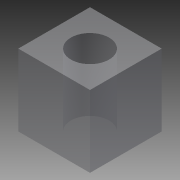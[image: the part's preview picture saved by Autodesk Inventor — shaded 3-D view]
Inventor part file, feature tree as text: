
AUTODESK INVENTOR PART (.ipt)
format: ipt  version: 2013 (Build 170138000, 138)  size: 76,800 bytes
history: native  units: in
note: dims shown in document units (in); Inventor stores cm internally (conversion verified against a paired STEP export)
features: extrude x1, sketch x1
ambient origin geometry x8: Origin, YZ Plane, XZ Plane, XY Plane, X Axis, Y Axis, Z Axis, Center Point
bodies: Solid1 (feature_tree)
feature tree (2):
  extrude  "Extrusion1"  Depth=0.5in
  sketch  "Sketch1"  dims[d0=0.5in d2=0.5in d3=0.266in d4=0.5in d5=0.0in]
